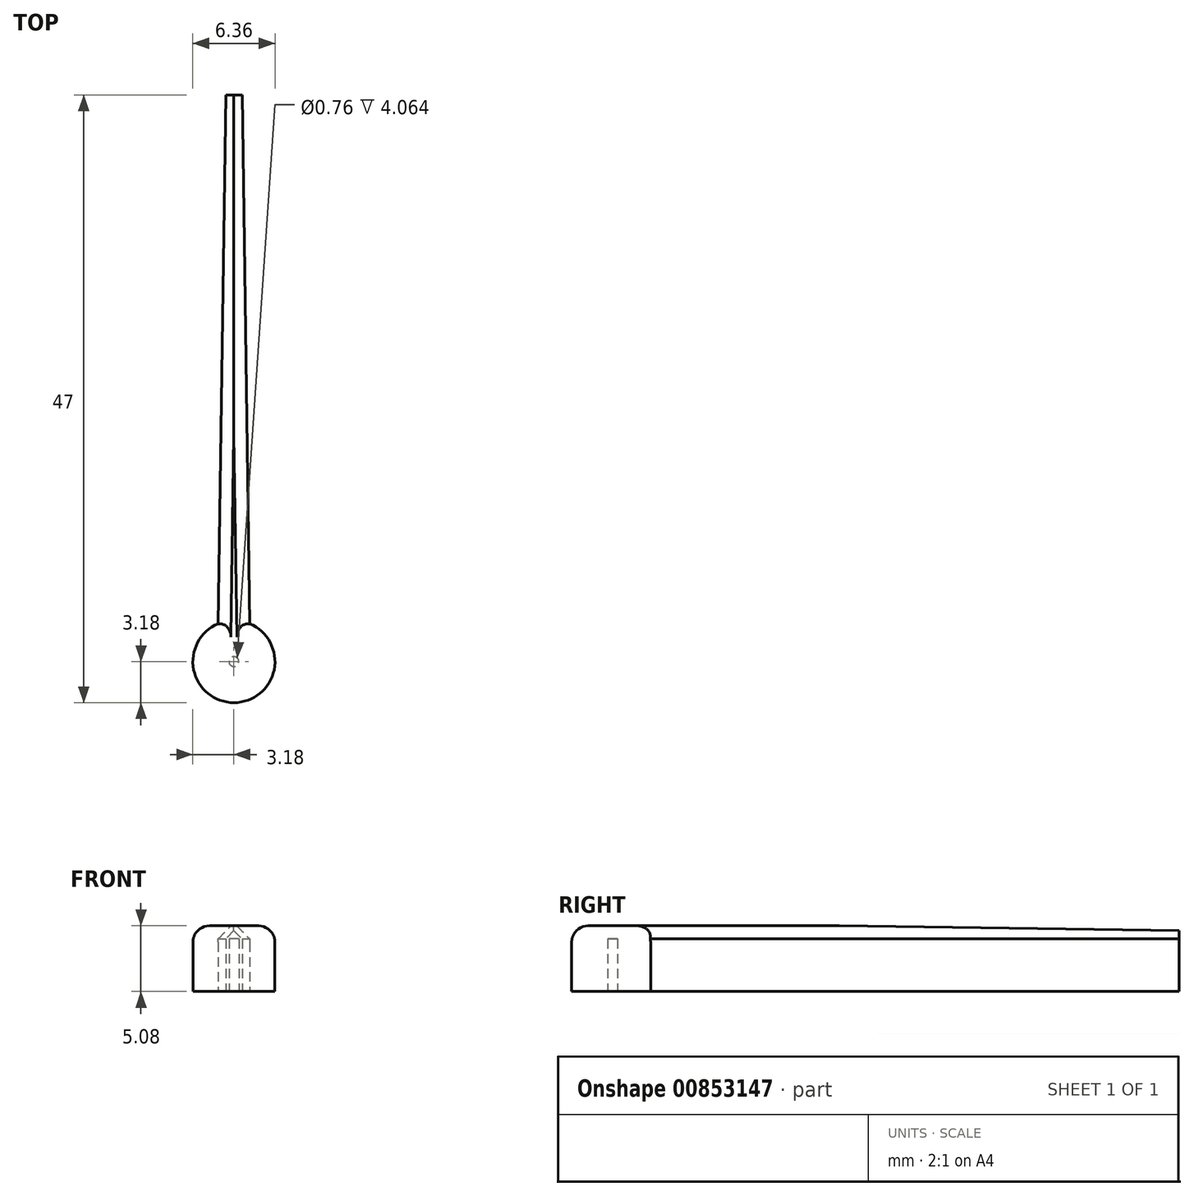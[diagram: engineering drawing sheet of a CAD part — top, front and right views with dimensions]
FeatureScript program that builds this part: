
annotation { "Feature Type Name" : "Feature", "Feature Type Description" : "" }
export const myFeature = defineFeature(function(context is Context, id is Id, definition is map)
    precondition{}
    {
        {
            var Q0;
            Q0=qCreatedBy(makeId("Top.planeOp"),FACE);
            var sketch = newSketch(context, id + "F0", { "sketchPlane" : qUnion([Q0])});
            skLineSegment(sketch, "E0", {"start": v(0, 0) * mm, "end": v(-1.27, 0) * mm});
            skLineSegment(sketch, "E1", {"start": v(0, 0) * mm, "end": v(1.27, 0) * mm});
            skCircle(sketch, "E2", {"center": v(0, 0) * mm, "radius": 3.18 * mm});
            skLineSegment(sketch, "E3", {"start": v(-1.27, 0) * mm, "end": v(-0.64, 43.82) * mm});
            skLineSegment(sketch, "E4", {"start": v(1.27, 0) * mm, "end": v(0.64, 43.81) * mm});
            skLineSegment(sketch, "E5", {"start": v(0.64, 43.81) * mm, "end": v(-0.64, 43.81) * mm});
            skSolve(sketch);
        }
        {
            var Q0;
            Q0=qSketchRegion(id+"F0",true);
            var Q1;
            {var subQ0=sQuery(id+"F0.wireOp",EDGE,"E1");var subQ1=sQuery(id+"F0.wireOp",EDGE,"E0");var subQ2=makeQuery(id+"F0.imprint","INTERSECT",VERTEX,{"derivedFrom":[subQ1,subQ0]});Q1=makeQuery(id+"F0.imprint","IMPRINT",FACE,{"disambiguationData":[TD([[makeQuery(id+"F0.imprint","IMPRINT",EDGE,{"disambiguationData":[TD([[subQ2,-1.0]])],"derivedFrom":subQ1}),-1.0]])]});}
            var Q2;
            {var subQ0=sQuery(id+"F0.wireOp",EDGE,"E1");var subQ1=sQuery(id+"F0.wireOp",EDGE,"E0");var subQ2=makeQuery(id+"F0.imprint","INTERSECT",VERTEX,{"derivedFrom":[subQ1,subQ0]});Q2=makeQuery(id+"F0.imprint","IMPRINT",FACE,{"disambiguationData":[TD([[makeQuery(id+"F0.imprint","IMPRINT",EDGE,{"disambiguationData":[TD([[subQ2,-1.0]])],"derivedFrom":subQ1}),1.0]])]});}
            extrude(context, id + "F1", {"entities" : qUnion([Q0, Q1, Q2]), "depth" : 5.08 * mm, "offsetDistance" : 25.4 * mm});
        }
        {
            var Q0;
            Q0=makeQuery(id+"F1.opExtrude","CAP_EDGE",EDGE,{"disambiguationData":[OSD([sQuery(id+"F0.wireOp",EDGE,"E4")])],"isStart":false});
            var Q1;
            Q1=makeQuery(id+"F1.opExtrude","CAP_EDGE",EDGE,{"disambiguationData":[OSD([sQuery(id+"F0.wireOp",EDGE,"E3")])],"isStart":false});
            var Q2;
            Q2=makeQuery(id+"F1.opExtrude","CAP_EDGE",EDGE,{"disambiguationData":[OSD([sQuery(id+"F0.wireOp",EDGE,"E5")])],"isStart":false});
            chamfer(context, id + "F2", {"entities" : qUnion([Q0, Q1, Q2]), "width" : 1.02 * mm, "tangentPropagation" : true});
        }
        {
            var Q0;
            Q0=makeQuery(id+"F1.opExtrude","CAP_EDGE",EDGE,{"disambiguationData":[OSD([sQuery(id+"F0.wireOp",EDGE,"E2")])],"isStart":false});
            fillet(context, id + "F3", {"entities" : qUnion([Q0]), "radius" : 1.27 * mm, "tangentPropagation" : true, "allowEdgeOverflow" : false});
        }
        {
            var Q0;
            Q0=qCreatedBy(makeId("Top.planeOp"),FACE);
            var sketch = newSketch(context, id + "F4", { "sketchPlane" : qUnion([Q0])});
            skCircle(sketch, "E6", {"center": v(0, 0) * mm, "radius": 0.38 * mm});
            skSolve(sketch);
        }
        {
            var Q0;
            Q0=qSketchRegion(id+"F4",true);
            extrude(context, id + "F5", {"entities" : qUnion([Q0]), "operationType" : NewBodyOperationType.REMOVE, "depth" : 4.06 * mm, "offsetDistance" : 25.4 * mm});
        }
    });
